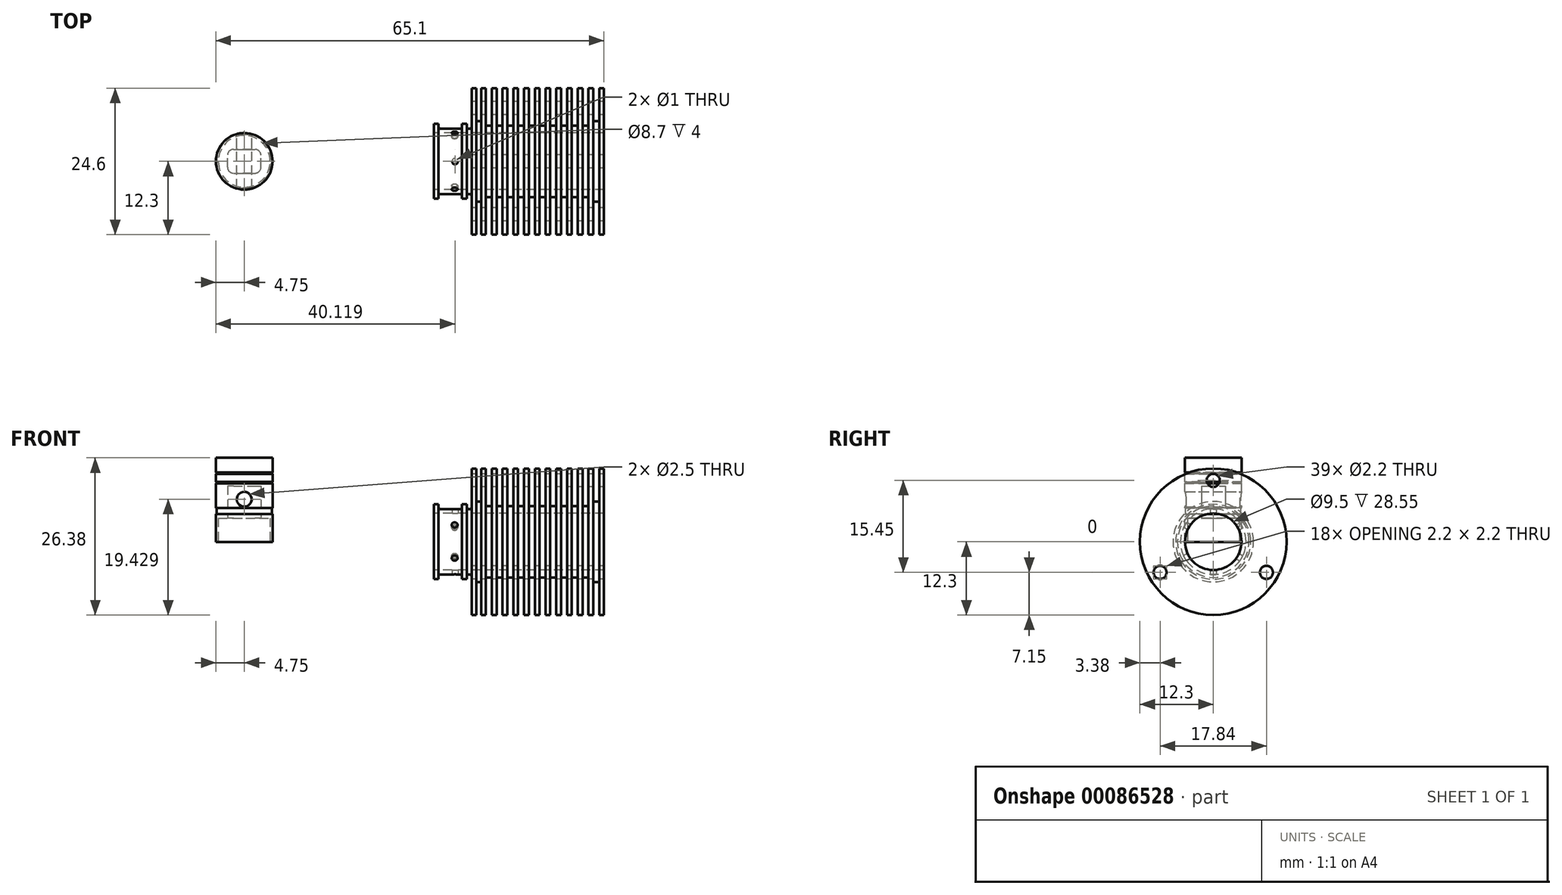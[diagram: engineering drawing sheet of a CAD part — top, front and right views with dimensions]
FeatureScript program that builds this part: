
annotation { "Feature Type Name" : "Feature", "Feature Type Description" : "" }
export const myFeature = defineFeature(function(context is Context, id is Id, definition is map)
    precondition{}
    {
        {
            var Q0;
            Q0=qCreatedBy(makeId("Front.planeOp"),FACE);
            var sketch = newSketch(context, id + "F0", { "sketchPlane" : qUnion([Q0])});
            skPoint(sketch, "E0.middle", {"position": v(0, 0) * mm});
            skLineSegment(sketch, "E1", {"start": v(0, -0.02) * mm, "end": v(0, 14.08) * mm});
            skLineSegment(sketch, "E2", {"start": v(-4.75, 14.08) * mm, "end": v(-4.75, 11.63) * mm});
            skLineSegment(sketch, "E3", {"start": v(-4.75, 4.68) * mm, "end": v(-4.62, 4.68) * mm});
            skLineSegment(sketch, "E4", {"start": v(-4.62, 4.68) * mm, "end": v(-4.62, 5.68) * mm});
            skLineSegment(sketch, "E5", {"start": v(-4.62, 5.68) * mm, "end": v(-4.75, 5.68) * mm});
            skLineSegment(sketch, "E6", {"start": v(-4.75, 10.03) * mm, "end": v(-4.62, 9.9) * mm});
            skLineSegment(sketch, "E7", {"start": v(-4.62, 9.9) * mm, "end": v(-4.75, 9.77) * mm});
            skLineSegment(sketch, "E8", {"start": v(-4.75, 11.63) * mm, "end": v(-4.62, 11.5) * mm});
            skLineSegment(sketch, "E9", {"start": v(-4.62, 11.5) * mm, "end": v(-4.75, 11.37) * mm});
            skLineSegment(sketch, "E10.trimOffspring", {"start": v(-4.75, 11.37) * mm, "end": v(-4.75, 10.03) * mm});
            skLineSegment(sketch, "E11.trimOffspring", {"start": v(-4.75, 9.77) * mm, "end": v(-4.75, 5.68) * mm});
            skLineSegment(sketch, "E12.trimOffspring", {"start": v(-4.75, 4.68) * mm, "end": v(-4.75, -0.02) * mm});
            skLineSegment(sketch, "E13", {"start": v(-4.75, 14.08) * mm, "end": v(0, 14.08) * mm});
            skLineSegment(sketch, "E14", {"start": v(-4.75, -0.02) * mm, "end": v(0, -0.02) * mm});
            skLineSegment(sketch, "E15", {"start": v(0, 14.08) * mm, "end": v(0, -6.41) * mm, "construction": true});
            skSolve(sketch);
        }
        {
            var Q0;
            {var subQ0=sQuery(id+"F0.wireOp",EDGE,"eGdi0r23-MWlI-d9Id-6IcZ-tQ7A4gUvsILz.left");Q0=makeQuery(id+"F0.imprint","IMPRINT",FACE,{"disambiguationData":[TD([[makeQuery(id+"F0.imprint","IMPRINT",EDGE,{"derivedFrom":subQ0}),1.0]])]});}
            var Q1;
            Q1=makeQuery(id+"F0.imprint","IMPRINT",FACE,{"disambiguationData":[TD([[makeQuery(id+"F0.imprint","IMPRINT",EDGE,{"derivedFrom":sQuery(id+"F0.wireOp",EDGE,"E1")}),1.0]])]});
            var Q2;
            Q2=sQuery(id+"F0.wireOp",EDGE,"E15");
            revolve(context, id + "F1", {"entities" : qUnion([Q0, Q1]), "axis" : qUnion([Q2]), "revolveType" : RevolveType.FULL});
        }
        {
            var Q0;
            Q0=qCreatedBy(makeId("Front.planeOp"),FACE);
            var sketch = newSketch(context, id + "F2", { "sketchPlane" : qUnion([Q0])});
            skPoint(sketch, "E16", {"position": v(0, 7.13) * mm});
            skCircle(sketch, "E17", {"center": v(0, 7.13) * mm, "radius": 1.25 * mm});
            skSolve(sketch);
        }
        {
            var Q0;
            Q0=makeQuery(id+"F2.imprint","IMPRINT",FACE,{"disambiguationData":[TD([[makeQuery(id+"F2.imprint","IMPRINT",EDGE,{"derivedFrom":sQuery(id+"F2.wireOp",EDGE,"E17")}),1.0]])]});
            extrude(context, id + "F3", {"entities" : qUnion([Q0]), "operationType" : NewBodyOperationType.REMOVE, "depth" : 10 * mm, "symmetric" : true});
        }
        {
            var Q0;
            Q0=makeQuery(id+"F1.opRevolve","SWEPT_FACE",FACE,{"disambiguationData":[OSD([sQuery(id+"F0.wireOp",EDGE,"E14")])]});
            var sketch = newSketch(context, id + "F4", { "sketchPlane" : qUnion([Q0])});
            skLineSegment(sketch, "E18.bottom", {"start": v(-1.8, 2) * mm, "end": v(1.8, 2) * mm});
            skLineSegment(sketch, "E18.top", {"start": v(-1.8, -2) * mm, "end": v(1.8, -2) * mm});
            skLineSegment(sketch, "E18.left", {"start": v(-2.8, 1) * mm, "end": v(-2.8, -1) * mm});
            skLineSegment(sketch, "E18.right", {"start": v(2.8, 1) * mm, "end": v(2.8, -1) * mm});
            skPoint(sketch, "E18.middle", {"position": v(0, 0) * mm});
            skCircle(sketch, "E19", {"center": v(0, 0) * mm, "radius": 4.35 * mm});
            skPoint(sketch, "E20.visualSharp", {"position": v(-2.8, 2) * mm});
            skArc(sketch, "E20.filletArc", {"start": v(-1.8, 2) * mm, "mid": v(-2.5, 1.7) * mm, "end": v(-2.8, 1) * mm});
            skPoint(sketch, "E21.visualSharp", {"position": v(-2.8, -2) * mm});
            skArc(sketch, "E21.filletArc", {"start": v(-2.8, -1) * mm, "mid": v(-2.5, -1.7) * mm, "end": v(-1.8, -2) * mm});
            skPoint(sketch, "E22.visualSharp", {"position": v(2.8, 2) * mm});
            skArc(sketch, "E22.filletArc", {"start": v(2.8, 1) * mm, "mid": v(2.5, 1.7) * mm, "end": v(1.8, 2) * mm});
            skPoint(sketch, "E23.visualSharp", {"position": v(2.8, -2) * mm});
            skArc(sketch, "E23.filletArc", {"start": v(1.8, -2) * mm, "mid": v(2.5, -1.7) * mm, "end": v(2.8, -1) * mm});
            skSolve(sketch);
        }
        {
            var Q0;
            Q0=makeQuery(id+"F4.imprint","IMPRINT",FACE,{"disambiguationData":[TD([[makeQuery(id+"F4.imprint","IMPRINT",EDGE,{"derivedFrom":sQuery(id+"F4.wireOp",EDGE,"E18.bottom")}),1.0]])]});
            var Q1;
            Q1=sQuery(id+"FsbAGgwMZmhRhTR_1.wireOp",EDGE,"XXkkC4YT-YGF8-Mw8t-M4hJ-ITye5uaQiXAc");
            extrude(context, id + "F5", {"entities" : qUnion([Q0]), "operationType" : NewBodyOperationType.REMOVE, "surfaceEntities" : qUnion([Q1]), "oppositeDirection" : true, "depth" : 4 * mm});
        }
        {
            var Q0;
            Q0=makeQuery(id+"F5.boolean.opBoolean","SPLIT",FACE,{"disambiguationData":[TD([makeQuery(id+"F5.opExtrude","SWEPT_FACE",FACE,{"disambiguationData":[OSD([sQuery(id+"F4.wireOp",EDGE,"E18.bottom")])]})])],"derivedFrom":makeQuery(id+"F1.opRevolve","SWEPT_FACE",FACE,{"disambiguationData":[OSD([sQuery(id+"F0.wireOp",EDGE,"E14")])]})});
            extrude(context, id + "F6", {"entities" : qUnion([Q0]), "operationType" : NewBodyOperationType.REMOVE, "oppositeDirection" : true, "depth" : 9.4 * mm});
        }
        {
            var Q0;
            Q0=qCreatedBy(makeId("Front.planeOp"),FACE);
            var sketch = newSketch(context, id + "F7", { "sketchPlane" : qUnion([Q0])});
            skPoint(sketch, "E24.0", {"position": v(0, 7.13) * mm});
            skCircle(sketch, "E24.1", {"center": v(0, 7.13) * mm, "radius": 1.25 * mm});
            skSolve(sketch);
        }
        {
            var Q0;
            Q0=makeQuery(id+"F7.imprint","IMPRINT",FACE,{"disambiguationData":[TD([[makeQuery(id+"F7.imprint","IMPRINT",EDGE,{"derivedFrom":sQuery(id+"F7.wireOp",EDGE,"E24.1")}),1.0]])]});
            extrude(context, id + "F8", {"entities" : qUnion([Q0]), "depth" : 9 * mm, "symmetric" : true});
        }
        {
            var Q0;
            Q0=qCreatedBy(makeId("Front.planeOp"),FACE);
            var sketch = newSketch(context, id + "F9", { "sketchPlane" : qUnion([Q0])});
            skLineSegment(sketch, "E25", {"start": v(27.89, 0) * mm, "end": v(63.64, 0) * mm, "construction": true});
            skLineSegment(sketch, "E26", {"start": v(31.8, 4.75) * mm, "end": v(60.35, 4.75) * mm});
            skLineSegment(sketch, "E27", {"start": v(60.35, 4.75) * mm, "end": v(60.35, 12.3) * mm});
            skLineSegment(sketch, "E28", {"start": v(59.55, 12.3) * mm, "end": v(59.55, 6.75) * mm});
            skLineSegment(sketch, "E29", {"start": v(59.55, 6.75) * mm, "end": v(58.55, 6.75) * mm});
            skLineSegment(sketch, "E30", {"start": v(60.35, 12.3) * mm, "end": v(59.55, 12.3) * mm});
            skLineSegment(sketch, "E31", {"start": v(40.24, 12.3) * mm, "end": v(39.75, 12.3) * mm});
            skLineSegment(sketch, "E32", {"start": v(39.75, 12.3) * mm, "end": v(39.75, 6.75) * mm});
            skLineSegment(sketch, "E33", {"start": v(38.95, 12.3) * mm, "end": v(38.15, 12.3) * mm});
            skLineSegment(sketch, "E34", {"start": v(38.15, 12.3) * mm, "end": v(38.15, 5.8) * mm});
            skLineSegment(sketch, "E35", {"start": v(38.95, 12.3) * mm, "end": v(38.95, 6.75) * mm});
            skLineSegment(sketch, "E36", {"start": v(38.95, 6.75) * mm, "end": v(39.75, 6.75) * mm});
            skLineSegment(sketch, "E37", {"start": v(31.8, 4.75) * mm, "end": v(31.8, 6.3) * mm});
            skLineSegment(sketch, "E38", {"start": v(31.8, 6.3) * mm, "end": v(32.6, 6.3) * mm});
            skLineSegment(sketch, "E39", {"start": v(32.6, 6.3) * mm, "end": v(32.6, 5.8) * mm});
            skLineSegment(sketch, "E40", {"start": v(32.9, 5.5) * mm, "end": v(36.25, 5.5) * mm});
            skLineSegment(sketch, "E41", {"start": v(36.55, 5.8) * mm, "end": v(36.55, 6.3) * mm});
            skLineSegment(sketch, "E42", {"start": v(36.55, 6.3) * mm, "end": v(37.35, 6.3) * mm});
            skLineSegment(sketch, "E43", {"start": v(37.35, 6.3) * mm, "end": v(37.35, 5.8) * mm});
            skLineSegment(sketch, "E44", {"start": v(37.65, 5.5) * mm, "end": v(37.85, 5.5) * mm});
            skLineSegment(sketch, "E45", {"start": v(58.55, 6.75) * mm, "end": v(58.55, 12.3) * mm});
            skLineSegment(sketch, "E46", {"start": v(58.55, 12.3) * mm, "end": v(57.75, 12.3) * mm});
            skLineSegment(sketch, "E47", {"start": v(57.75, 12.3) * mm, "end": v(57.75, 6) * mm});
            skLineSegment(sketch, "E48", {"start": v(57.75, 6) * mm, "end": v(56.75, 6) * mm});
            skLineSegment(sketch, "E49", {"start": v(56.75, 6) * mm, "end": v(56.75, 12.3) * mm});
            skLineSegment(sketch, "E50", {"start": v(56.75, 12.3) * mm, "end": v(55.95, 12.3) * mm});
            skLineSegment(sketch, "E51", {"start": v(55.95, 12.3) * mm, "end": v(55.95, 6) * mm});
            skLineSegment(sketch, "E52.1.0.0", {"start": v(55.95, 6) * mm, "end": v(54.95, 6) * mm});
            skLineSegment(sketch, "E52.1.0.1", {"start": v(54.95, 6) * mm, "end": v(54.95, 12.3) * mm});
            skLineSegment(sketch, "E52.1.0.2", {"start": v(54.95, 12.3) * mm, "end": v(54.15, 12.3) * mm});
            skLineSegment(sketch, "E52.1.0.3", {"start": v(54.15, 12.3) * mm, "end": v(54.15, 6) * mm});
            skLineSegment(sketch, "E52.2.0.0", {"start": v(54.15, 6) * mm, "end": v(53.15, 6) * mm});
            skLineSegment(sketch, "E52.2.0.1", {"start": v(53.15, 6) * mm, "end": v(53.15, 12.3) * mm});
            skLineSegment(sketch, "E52.2.0.2", {"start": v(53.15, 12.3) * mm, "end": v(52.35, 12.3) * mm});
            skLineSegment(sketch, "E52.2.0.3", {"start": v(52.35, 12.3) * mm, "end": v(52.35, 6) * mm});
            skLineSegment(sketch, "E52.3.0.0", {"start": v(52.35, 6) * mm, "end": v(51.35, 6) * mm});
            skLineSegment(sketch, "E52.3.0.1", {"start": v(51.35, 6) * mm, "end": v(51.35, 12.3) * mm});
            skLineSegment(sketch, "E52.3.0.2", {"start": v(51.35, 12.3) * mm, "end": v(50.55, 12.3) * mm});
            skLineSegment(sketch, "E52.3.0.3", {"start": v(50.55, 12.3) * mm, "end": v(50.55, 6) * mm});
            skLineSegment(sketch, "E52.4.0.0", {"start": v(50.55, 6) * mm, "end": v(49.55, 6) * mm});
            skLineSegment(sketch, "E52.4.0.1", {"start": v(49.55, 6) * mm, "end": v(49.55, 12.3) * mm});
            skLineSegment(sketch, "E52.4.0.2", {"start": v(49.55, 12.3) * mm, "end": v(48.75, 12.3) * mm});
            skLineSegment(sketch, "E52.4.0.3", {"start": v(48.75, 12.3) * mm, "end": v(48.75, 6) * mm});
            skLineSegment(sketch, "E52.5.0.0", {"start": v(48.75, 6) * mm, "end": v(47.75, 6) * mm});
            skLineSegment(sketch, "E52.5.0.1", {"start": v(47.75, 6) * mm, "end": v(47.75, 12.3) * mm});
            skLineSegment(sketch, "E52.5.0.2", {"start": v(47.75, 12.3) * mm, "end": v(46.95, 12.3) * mm});
            skLineSegment(sketch, "E52.5.0.3", {"start": v(46.95, 12.3) * mm, "end": v(46.95, 6) * mm});
            skLineSegment(sketch, "E52.6.0.0", {"start": v(46.95, 6) * mm, "end": v(45.95, 6) * mm});
            skLineSegment(sketch, "E52.6.0.1", {"start": v(45.95, 6) * mm, "end": v(45.95, 12.3) * mm});
            skLineSegment(sketch, "E52.6.0.2", {"start": v(45.95, 12.3) * mm, "end": v(45.15, 12.3) * mm});
            skLineSegment(sketch, "E52.6.0.3", {"start": v(45.15, 12.3) * mm, "end": v(45.15, 6) * mm});
            skLineSegment(sketch, "E52.7.0.0", {"start": v(45.15, 6) * mm, "end": v(44.15, 6) * mm});
            skLineSegment(sketch, "E52.7.0.1", {"start": v(44.15, 6) * mm, "end": v(44.15, 12.3) * mm});
            skLineSegment(sketch, "E52.7.0.2", {"start": v(44.15, 12.3) * mm, "end": v(43.35, 12.3) * mm});
            skLineSegment(sketch, "E52.7.0.3", {"start": v(43.35, 12.3) * mm, "end": v(43.35, 6) * mm});
            skLineSegment(sketch, "E52.8.0.0", {"start": v(43.35, 6) * mm, "end": v(42.35, 6) * mm});
            skLineSegment(sketch, "E52.8.0.1", {"start": v(42.35, 6) * mm, "end": v(42.35, 12.3) * mm});
            skLineSegment(sketch, "E52.8.0.2", {"start": v(42.35, 12.3) * mm, "end": v(41.55, 12.3) * mm});
            skLineSegment(sketch, "E52.8.0.3", {"start": v(41.55, 12.3) * mm, "end": v(41.55, 6) * mm});
            skLineSegment(sketch, "E52.9.0.0", {"start": v(41.55, 6) * mm, "end": v(40.55, 6) * mm});
            skLineSegment(sketch, "E52.9.0.1", {"start": v(40.55, 6) * mm, "end": v(40.55, 12.3) * mm});
            skLineSegment(sketch, "E52.9.0.2", {"start": v(40.55, 12.3) * mm, "end": v(39.75, 12.3) * mm});
            skLineSegment(sketch, "E52.9.0.3", {"start": v(39.75, 12.3) * mm, "end": v(39.75, 6) * mm});
            skLineSegment(sketch, "E52.direction1", {"start": v(56.75, 6) * mm, "end": v(54.95, 6) * mm, "construction": true});
            skPoint(sketch, "E53.visualSharp", {"position": v(37.35, 5.5) * mm});
            skArc(sketch, "E53.filletArc", {"start": v(37.35, 5.8) * mm, "mid": v(37.44, 5.59) * mm, "end": v(37.65, 5.5) * mm});
            skPoint(sketch, "E54.visualSharp", {"position": v(32.6, 5.5) * mm});
            skArc(sketch, "E54.filletArc", {"start": v(32.6, 5.8) * mm, "mid": v(32.69, 5.59) * mm, "end": v(32.9, 5.5) * mm});
            skPoint(sketch, "E55.visualSharp", {"position": v(38.15, 5.5) * mm});
            skArc(sketch, "E55.filletArc", {"start": v(37.85, 5.5) * mm, "mid": v(38.06, 5.59) * mm, "end": v(38.15, 5.8) * mm});
            skPoint(sketch, "E56.visualSharp", {"position": v(36.55, 5.5) * mm});
            skArc(sketch, "E56.filletArc", {"start": v(36.25, 5.5) * mm, "mid": v(36.46, 5.59) * mm, "end": v(36.55, 5.8) * mm});
            skPoint(sketch, "E57", {"position": v(35.3, 5.5) * mm});
            skSolve(sketch);
        }
        {
            var Q0;
            {var subQ0=sQuery(id+"F9.wireOp",EDGE,"E27");Q0=makeQuery(id+"F9.imprint","IMPRINT",FACE,{"disambiguationData":[TD([[makeQuery(id+"F9.imprint","IMPRINT",EDGE,{"derivedFrom":subQ0}),1.0]])]});}
            var Q1;
            Q1=sQuery(id+"F9.wireOp",EDGE,"E25");
            revolve(context, id + "F10", {"entities" : qUnion([Q0]), "axis" : qUnion([Q1]), "revolveType" : RevolveType.FULL});
        }
        {
            var Q0;
            Q0=makeQuery(id+"F10.opRevolve","SWEPT_FACE",FACE,{"disambiguationData":[OSD([sQuery(id+"F9.wireOp",EDGE,"E27")])]});
            var sketch = newSketch(context, id + "F11", { "sketchPlane" : qUnion([Q0])});
            skCircle(sketch, "E58", {"center": v(0, 0) * mm, "radius": 10.3 * mm, "construction": true});
            skPoint(sketch, "E59", {"position": v(0, 10.3) * mm});
            skPoint(sketch, "E60.1.1", {"position": v(-8.92, -5.15) * mm});
            skPoint(sketch, "E60.2.1", {"position": v(8.92, -5.15) * mm});
            skSolve(sketch);
        }
        {
            var Q0;
            Q0=sQuery(id+"F11.wireOp",VERTEX,"E59");
            var Q1;
            Q1=sQuery(id+"F11.wireOp",VERTEX,"E60.1.1");
            var Q2;
            Q2=sQuery(id+"F11.wireOp",VERTEX,"E60.2.1");
            var Q3;
            Q3=makeQuery(id+"F10.opRevolve","SWEPT_BODY",BODY,{"disambiguationData":[OSD([sQuery(id+"F9.wireOp",EDGE,"E26"),sQuery(id+"F9.wireOp",EDGE,"E27"),sQuery(id+"F9.wireOp",EDGE,"E28"),sQuery(id+"F9.wireOp",EDGE,"E29"),sQuery(id+"F9.wireOp",EDGE,"E30"),sQuery(id+"F9.wireOp",EDGE,"E33"),sQuery(id+"F9.wireOp",EDGE,"E34"),sQuery(id+"F9.wireOp",EDGE,"E35"),sQuery(id+"F9.wireOp",EDGE,"E36"),sQuery(id+"F9.wireOp",EDGE,"E37"),sQuery(id+"F9.wireOp",EDGE,"E38"),sQuery(id+"F9.wireOp",EDGE,"E39"),sQuery(id+"F9.wireOp",EDGE,"E40"),sQuery(id+"F9.wireOp",EDGE,"E41"),sQuery(id+"F9.wireOp",EDGE,"E42"),sQuery(id+"F9.wireOp",EDGE,"E43"),sQuery(id+"F9.wireOp",EDGE,"E44"),sQuery(id+"F9.wireOp",EDGE,"E45"),sQuery(id+"F9.wireOp",EDGE,"E46"),sQuery(id+"F9.wireOp",EDGE,"E47"),sQuery(id+"F9.wireOp",EDGE,"E48"),sQuery(id+"F9.wireOp",EDGE,"E49"),sQuery(id+"F9.wireOp",EDGE,"E50"),sQuery(id+"F9.wireOp",EDGE,"E51"),sQuery(id+"F9.wireOp",EDGE,"E52.1.0.0"),sQuery(id+"F9.wireOp",EDGE,"E52.1.0.1"),sQuery(id+"F9.wireOp",EDGE,"E52.1.0.2"),sQuery(id+"F9.wireOp",EDGE,"E52.1.0.3"),sQuery(id+"F9.wireOp",EDGE,"E52.2.0.0"),sQuery(id+"F9.wireOp",EDGE,"E52.2.0.1"),sQuery(id+"F9.wireOp",EDGE,"E52.2.0.2"),sQuery(id+"F9.wireOp",EDGE,"E52.2.0.3"),sQuery(id+"F9.wireOp",EDGE,"E52.3.0.0"),sQuery(id+"F9.wireOp",EDGE,"E52.3.0.1"),sQuery(id+"F9.wireOp",EDGE,"E52.3.0.2"),sQuery(id+"F9.wireOp",EDGE,"E52.3.0.3"),sQuery(id+"F9.wireOp",EDGE,"E52.4.0.0"),sQuery(id+"F9.wireOp",EDGE,"E52.4.0.1"),sQuery(id+"F9.wireOp",EDGE,"E52.4.0.2"),sQuery(id+"F9.wireOp",EDGE,"E52.4.0.3"),sQuery(id+"F9.wireOp",EDGE,"E52.5.0.0"),sQuery(id+"F9.wireOp",EDGE,"E52.5.0.1"),sQuery(id+"F9.wireOp",EDGE,"E52.5.0.2"),sQuery(id+"F9.wireOp",EDGE,"E52.5.0.3"),sQuery(id+"F9.wireOp",EDGE,"E52.6.0.0"),sQuery(id+"F9.wireOp",EDGE,"E52.6.0.1"),sQuery(id+"F9.wireOp",EDGE,"E52.6.0.2"),sQuery(id+"F9.wireOp",EDGE,"E52.6.0.3"),sQuery(id+"F9.wireOp",EDGE,"E52.7.0.0"),sQuery(id+"F9.wireOp",EDGE,"E52.7.0.1"),sQuery(id+"F9.wireOp",EDGE,"E52.7.0.2"),sQuery(id+"F9.wireOp",EDGE,"E52.7.0.3"),sQuery(id+"F9.wireOp",EDGE,"E52.8.0.0"),sQuery(id+"F9.wireOp",EDGE,"E52.8.0.1"),sQuery(id+"F9.wireOp",EDGE,"E52.8.0.2"),sQuery(id+"F9.wireOp",EDGE,"E52.8.0.3"),sQuery(id+"F9.wireOp",EDGE,"E52.9.0.0"),sQuery(id+"F9.wireOp",EDGE,"E52.9.0.1"),sQuery(id+"F9.wireOp",EDGE,"E52.9.0.2"),sQuery(id+"F9.wireOp",EDGE,"E52.9.0.3"),sQuery(id+"F9.wireOp",EDGE,"E53.filletArc"),sQuery(id+"F9.wireOp",EDGE,"E54.filletArc"),sQuery(id+"F9.wireOp",EDGE,"E55.filletArc"),sQuery(id+"F9.wireOp",EDGE,"E56.filletArc")])]});
            hole(context, id + "F12", {"style" : HoleStyle.SIMPLE, "endStyle" : HoleEndStyle.THROUGH, "holeDiameter" : 2.2 * mm, "startFromSketch" : true, "locations" : qUnion([Q0, Q1, Q2]), "scope" : qUnion([Q3]), "isTappedThrough" : true});
        }
        {
            var Q0;
            Q0=qCreatedBy(makeId("Top.planeOp"),FACE);
            var sketch = newSketch(context, id + "F13", { "sketchPlane" : qUnion([Q0])});
            skCircle(sketch, "E61", {"center": v(35.37, 0) * mm, "radius": 0.5 * mm});
            skSolve(sketch);
        }
        {
            var Q0;
            Q0=qSketchRegion(id+"F13",true);
            var Q1;
            Q1=sQuery(id+"F13.wireOp",EDGE,"E61");
            extrude(context, id + "F14", {"entities" : qUnion([Q0]), "operationType" : NewBodyOperationType.REMOVE, "surfaceEntities" : qUnion([Q1]), "depth" : 13 * mm, "symmetric" : true});
        }
        {
            var Q0;
            Q0=qCreatedBy(makeId("Front.planeOp"),FACE);
            var Q1;
            Q1=sQuery(id+"F9.wireOp",EDGE,"E25");
            cPlane(context, id + "F15", {"entities" : qUnion([Q0, Q1]), "cplaneType" : CPlaneType.LINE_ANGLE, "offset" : 150 * mm, "angle" : 30 * degree, "width" : 150 * mm, "height" : 150 * mm});
        }
        {
            var Q0;
            Q0=qCreatedBy(id+"F15.planeOp",FACE);
            var sketch = newSketch(context, id + "F16", { "sketchPlane" : qUnion([Q0])});
            skPoint(sketch, "E62", {"position": v(-35.3, 0) * mm});
            skCircle(sketch, "E63", {"center": v(-35.3, 0) * mm, "radius": 0.5 * mm});
            skSolve(sketch);
        }
        {
            var Q0;
            Q0=qSketchRegion(id+"F16",true);
            var Q1;
            Q1=sQuery(id+"F16.wireOp",EDGE,"E63");
            extrude(context, id + "F17", {"entities" : qUnion([Q0]), "operationType" : NewBodyOperationType.REMOVE, "surfaceEntities" : qUnion([Q1]), "depth" : 13 * mm, "symmetric" : true});
        }
        {
            var Q0;
            Q0=qCreatedBy(makeId("Top.planeOp"),FACE);
            var Q1;
            Q1=sQuery(id+"F9.wireOp",EDGE,"E25");
            cPlane(context, id + "F18", {"entities" : qUnion([Q0, Q1]), "cplaneType" : CPlaneType.LINE_ANGLE, "offset" : 150 * mm, "angle" : 59 * degree, "width" : 150 * mm, "height" : 150 * mm});
        }
        {
            var Q0;
            Q0=qCreatedBy(id+"F18.planeOp",FACE);
            var sketch = newSketch(context, id + "F19", { "sketchPlane" : qUnion([Q0])});
            skPoint(sketch, "E64", {"position": v(-35.3, 0) * mm});
            skCircle(sketch, "E65", {"center": v(-35.3, 0) * mm, "radius": 0.5 * mm});
            skSolve(sketch);
        }
        {
            var Q0;
            Q0=qSketchRegion(id+"F19",true);
            var Q1;
            Q1=sQuery(id+"F19.wireOp",EDGE,"E65");
            extrude(context, id + "F20", {"entities" : qUnion([Q0]), "operationType" : NewBodyOperationType.REMOVE, "surfaceEntities" : qUnion([Q1]), "depth" : 13 * mm, "symmetric" : true});
        }
    });
